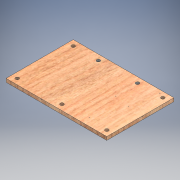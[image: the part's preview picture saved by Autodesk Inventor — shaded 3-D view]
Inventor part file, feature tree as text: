
AUTODESK INVENTOR PART (.ipt)
format: ipt  version: 2018 (Build 220112000, 112)  size: 136,704 bytes
history: native  units: mm
features: extrude x1
ambient origin geometry x8: Origin, YZ Plane, XZ Plane, XY Plane, X Axis, Y Axis, Z Axis, Center Point
bodies: Solid1 (feature_tree)
feature tree (1):
  extrude  "Extrusion1"  Depth=140.0mm
